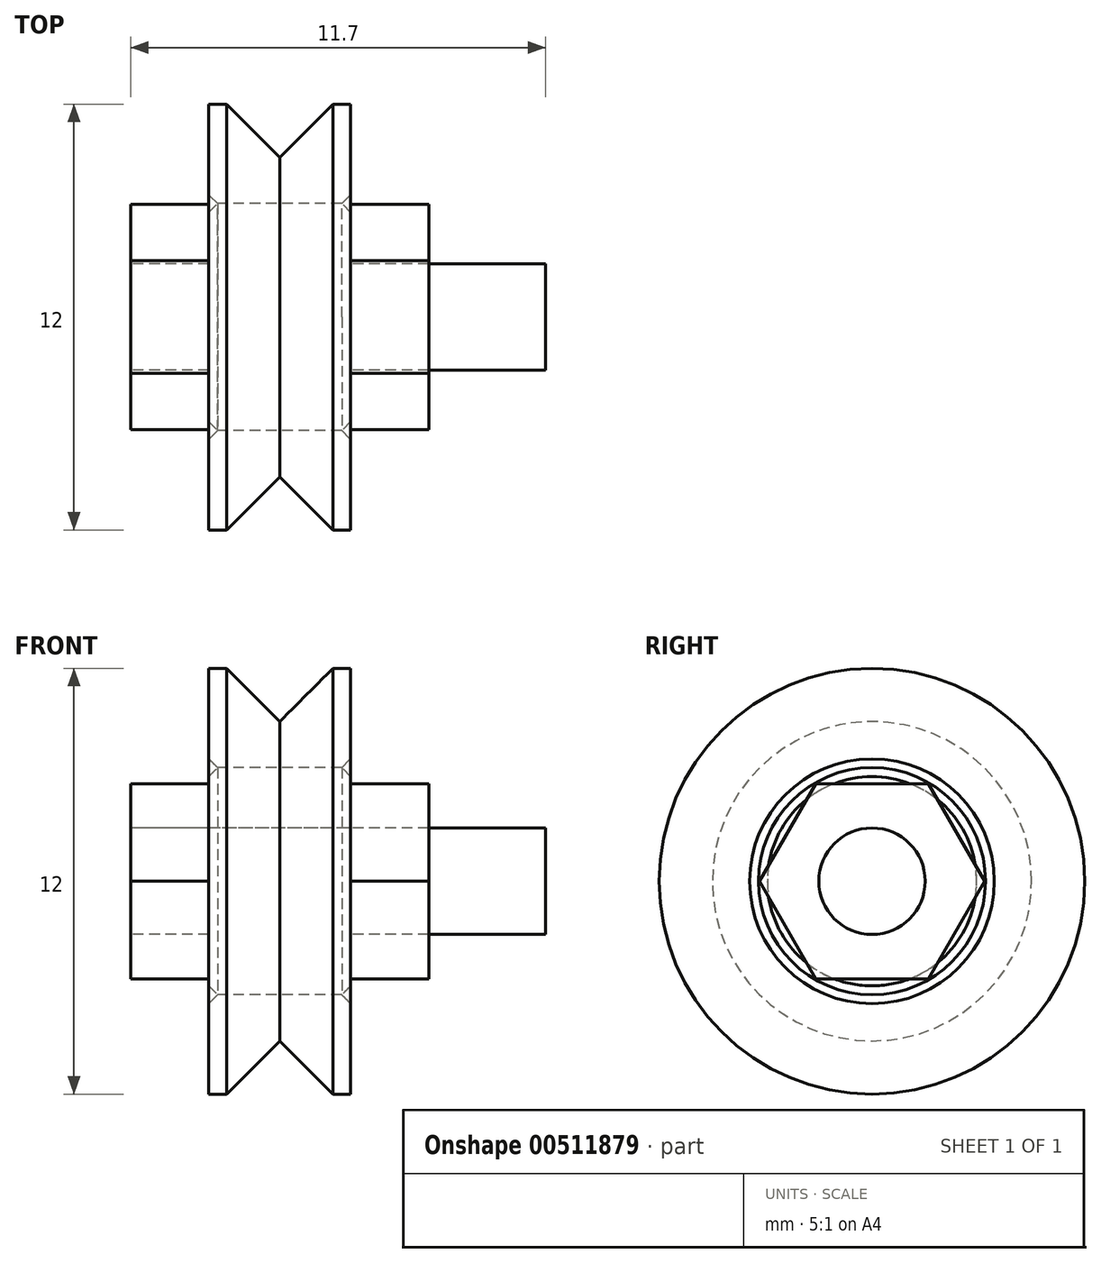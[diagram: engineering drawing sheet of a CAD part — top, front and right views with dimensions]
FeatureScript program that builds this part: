
annotation { "Feature Type Name" : "Feature", "Feature Type Description" : "" }
export const myFeature = defineFeature(function(context is Context, id is Id, definition is map)
    precondition{}
    {
        {
            var Q0;
            Q0=qCreatedBy(makeId("Front.planeOp"),FACE);
            var sketch = newSketch(context, id + "F0", { "sketchPlane" : qUnion([Q0])});
            skLineSegment(sketch, "E0", {"start": v(0, 5.5) * mm, "end": v(0, -5.5) * mm});
            skLineSegment(sketch, "E1", {"start": v(0, -5.5) * mm, "end": v(-2.5, -5.5) * mm});
            skLineSegment(sketch, "E2", {"start": v(-2.5, -5.5) * mm, "end": v(-2.5, -2.4) * mm});
            skLineSegment(sketch, "E3", {"start": v(-3.8, -2.4) * mm, "end": v(-3.8, -2.8) * mm});
            skLineSegment(sketch, "E4", {"start": v(-3.8, -2.8) * mm, "end": v(-6.3, -2.8) * mm});
            skArc(sketch, "E5", {"start": v(-2.5, -2.4) * mm, "mid": v(-3.15, -1.75) * mm, "end": v(-3.8, -2.4) * mm});
            skLineSegment(sketch, "E6.MirrorCS", {"start": v(-3.8, 2.8) * mm, "end": v(-6.3, 2.8) * mm});
            skLineSegment(sketch, "E7.MirrorCS", {"start": v(-3.8, 2.4) * mm, "end": v(-3.8, 2.8) * mm});
            skArc(sketch, "E8.MirrorCS", {"start": v(-2.5, 2.4) * mm, "mid": v(-3.15, 1.75) * mm, "end": v(-3.8, 2.4) * mm});
            skLineSegment(sketch, "E9.MirrorCS", {"start": v(-2.5, 5.5) * mm, "end": v(-2.5, 2.4) * mm});
            skLineSegment(sketch, "E10.MirrorCS", {"start": v(0, 5.5) * mm, "end": v(-2.5, 5.5) * mm});
            skLineSegment(sketch, "E11", {"start": v(-6.3, 2.8) * mm, "end": v(-6.3, -2.8) * mm});
            skLineSegment(sketch, "E12", {"start": v(0, 0) * mm, "end": v(11.7, 0) * mm});
            skLineSegment(sketch, "E13", {"start": v(11.7, 0) * mm, "end": v(11.7, 1.5) * mm});
            skLineSegment(sketch, "E14", {"start": v(11.7, 1.5) * mm, "end": v(0, 1.5) * mm});
            skLineSegment(sketch, "E15", {"start": v(2.2, 1.5) * mm, "end": v(2.2, 6) * mm});
            skLineSegment(sketch, "E16", {"start": v(2.2, 6) * mm, "end": v(2.7, 6) * mm});
            skLineSegment(sketch, "E17", {"start": v(2.7, 6) * mm, "end": v(4.2, 4.5) * mm});
            skLineSegment(sketch, "E18", {"start": v(4.2, 4.5) * mm, "end": v(5.7, 6) * mm});
            skLineSegment(sketch, "E19", {"start": v(5.7, 6) * mm, "end": v(6.2, 6) * mm});
            skLineSegment(sketch, "E20", {"start": v(6.2, 6) * mm, "end": v(6.2, 1.5) * mm});
            skLineSegment(sketch, "E21", {"start": v(4.2, 4.5) * mm, "end": v(4.2, 1.5) * mm, "construction": true});
            skLineSegment(sketch, "E22", {"start": v(2.2, 3.2) * mm, "end": v(6.2, 3.2) * mm});
            skSolve(sketch);
        }
        {
            var Q0;
            {var subQ1=sQuery(id+"F0.wireOp",EDGE,"E12");Q0=makeQuery(id+"F0.imprint","IMPRINT",FACE,{"disambiguationData":[TD([[makeQuery(id+"F0.imprint","IMPRINT",EDGE,{"derivedFrom":subQ1}),1.0]])]});}
            var Q1;
            Q1=sQuery(id+"F0.wireOp",EDGE,"E12");
            revolve(context, id + "F1", {"entities" : qUnion([Q0]), "axis" : qUnion([Q1]), "revolveType" : RevolveType.FULL});
        }
        {
            var Q0;
            {var subQ5=sQuery(id+"F0.wireOp",EDGE,"E22");Q0=makeQuery(id+"F0.imprint","IMPRINT",FACE,{"disambiguationData":[TD([[makeQuery(id+"F0.imprint","IMPRINT",EDGE,{"derivedFrom":subQ5}),-1.0]])]});}
            var Q1;
            Q1=sQuery(id+"F0.wireOp",EDGE,"E12");
            revolve(context, id + "F2", {"entities" : qUnion([Q0]), "axis" : qUnion([Q1]), "revolveType" : RevolveType.FULL});
        }
        {
            var Q0;
            {var subQ0=sQuery(id+"F0.wireOp",EDGE,"E16");Q0=makeQuery(id+"F0.imprint","IMPRINT",FACE,{"disambiguationData":[TD([[makeQuery(id+"F0.imprint","IMPRINT",EDGE,{"derivedFrom":subQ0}),-1.0]])]});}
            var Q1;
            Q1=sQuery(id+"F0.wireOp",EDGE,"E12");
            revolve(context, id + "F3", {"entities" : qUnion([Q0]), "axis" : qUnion([Q1]), "revolveType" : RevolveType.FULL});
        }
        {
            var Q0;
            Q0=makeQuery(id+"F2.opRevolve","SWEPT_EDGE",EDGE,{"disambiguationData":[OSD([sQuery(id+"F0.wireOp",EDGE,"E15"),sQuery(id+"F0.wireOp",EDGE,"E22")])]});
            var Q1;
            Q1=makeQuery(id+"F3.opRevolve","SWEPT_EDGE",EDGE,{"disambiguationData":[OSD([sQuery(id+"F0.wireOp",EDGE,"E15"),sQuery(id+"F0.wireOp",EDGE,"E22")])]});
            var Q2;
            Q2=makeQuery(id+"F2.opRevolve","SWEPT_EDGE",EDGE,{"disambiguationData":[OSD([sQuery(id+"F0.wireOp",EDGE,"E20"),sQuery(id+"F0.wireOp",EDGE,"E22")])]});
            var Q3;
            Q3=makeQuery(id+"F3.opRevolve","SWEPT_EDGE",EDGE,{"disambiguationData":[OSD([sQuery(id+"F0.wireOp",EDGE,"E20"),sQuery(id+"F0.wireOp",EDGE,"E22")])]});
            chamfer(context, id + "F4", {"entities" : qUnion([Q0, Q1, Q2, Q3]), "width" : 0.25 * mm, "tangentPropagation" : true});
        }
        {
            var Q0;
            {var subQ4=sQuery(id+"F0.wireOp",EDGE,"E1");Q0=makeQuery(id+"F0.imprint","IMPRINT",FACE,{"disambiguationData":[TD([[makeQuery(id+"F0.imprint","IMPRINT",EDGE,{"derivedFrom":subQ4}),-1.0]])]});}
            extrude(context, id + "F5", {"entities" : qUnion([Q0]), "depth" : 25 * mm, "offsetDistance" : 25 * mm, "symmetric" : true});
        }
        {
            var Q0;
            Q0=qCreatedBy(makeId("Right.planeOp"),FACE);
            var sketch = newSketch(context, id + "F6", { "sketchPlane" : qUnion([Q0])});
            skCircle(sketch, "E23.cCircle", {"center": v(0, 0) * mm, "radius": 2.75 * mm, "construction": true});
            skLineSegment(sketch, "E23.0", {"start": v(-1.59, 2.75) * mm, "end": v(1.59, 2.75) * mm});
            skLineSegment(sketch, "E23.1", {"start": v(1.59, 2.75) * mm, "end": v(3.18, 0) * mm});
            skLineSegment(sketch, "E23.2", {"start": v(3.18, 0) * mm, "end": v(1.59, -2.75) * mm});
            skLineSegment(sketch, "E23.3", {"start": v(1.59, -2.75) * mm, "end": v(-1.59, -2.75) * mm});
            skLineSegment(sketch, "E23.4", {"start": v(-1.59, -2.75) * mm, "end": v(-3.18, 0) * mm});
            skLineSegment(sketch, "E23.5", {"start": v(-3.18, 0) * mm, "end": v(-1.59, 2.75) * mm});
            skPoint(sketch, "E23.0.midPoint", {"position": v(0, 2.75) * mm});
            skCircle(sketch, "E24.0", {"center": v(0, 0) * mm, "radius": 1.5 * mm});
            skSolve(sketch);
        }
        {
            var Q0;
            Q0=makeQuery(id+"F6.imprint","IMPRINT",FACE,{"disambiguationData":[TD([[makeQuery(id+"F6.imprint","IMPRINT",EDGE,{"derivedFrom":sQuery(id+"F6.wireOp",EDGE,"E23.0")}),-1.0]])]});
            extrude(context, id + "F7", {"entities" : qUnion([Q0]), "depth" : 2.2 * mm});
        }
        {
            var Q0;
            Q0=makeQuery(id+"F7.opExtrude","SWEPT_BODY",BODY,{"disambiguationData":[OSD([sQuery(id+"F6.wireOp",EDGE,"E23.0"),sQuery(id+"F6.wireOp",EDGE,"E23.1"),sQuery(id+"F6.wireOp",EDGE,"E23.2"),sQuery(id+"F6.wireOp",EDGE,"E23.3"),sQuery(id+"F6.wireOp",EDGE,"E23.4"),sQuery(id+"F6.wireOp",EDGE,"E23.5"),sQuery(id+"F6.wireOp",EDGE,"E24.0")])]});
            var Q1;
            Q1=qCreatedBy(makeId("Right.planeOp"),FACE);
            transform(context, id + "F8", {"entities" : qUnion([Q0]), "transformType" : TransformType.TRANSLATION_DISTANCE, "transformDirection" : qUnion([Q1]), "distance" : (2.2 + 4) * mm, "makeCopy" : true});
        }
        {
            var Q0;
            Q0=makeQuery(id+"F5.opExtrude","SWEPT_BODY",BODY,{"disambiguationData":[OSD([sQuery(id+"F0.wireOp",EDGE,"E0"),sQuery(id+"F0.wireOp",EDGE,"E1"),sQuery(id+"F0.wireOp",EDGE,"E2"),sQuery(id+"F0.wireOp",EDGE,"E3"),sQuery(id+"F0.wireOp",EDGE,"E4"),sQuery(id+"F0.wireOp",EDGE,"E5"),sQuery(id+"F0.wireOp",EDGE,"E6.MirrorCS"),sQuery(id+"F0.wireOp",EDGE,"E7.MirrorCS"),sQuery(id+"F0.wireOp",EDGE,"E8.MirrorCS"),sQuery(id+"F0.wireOp",EDGE,"E9.MirrorCS"),sQuery(id+"F0.wireOp",EDGE,"E10.MirrorCS"),sQuery(id+"F0.wireOp",EDGE,"E11")])]});
            deleteBodies(context, id + "F9", {"entities" : qUnion([Q0])});
        }
    });
